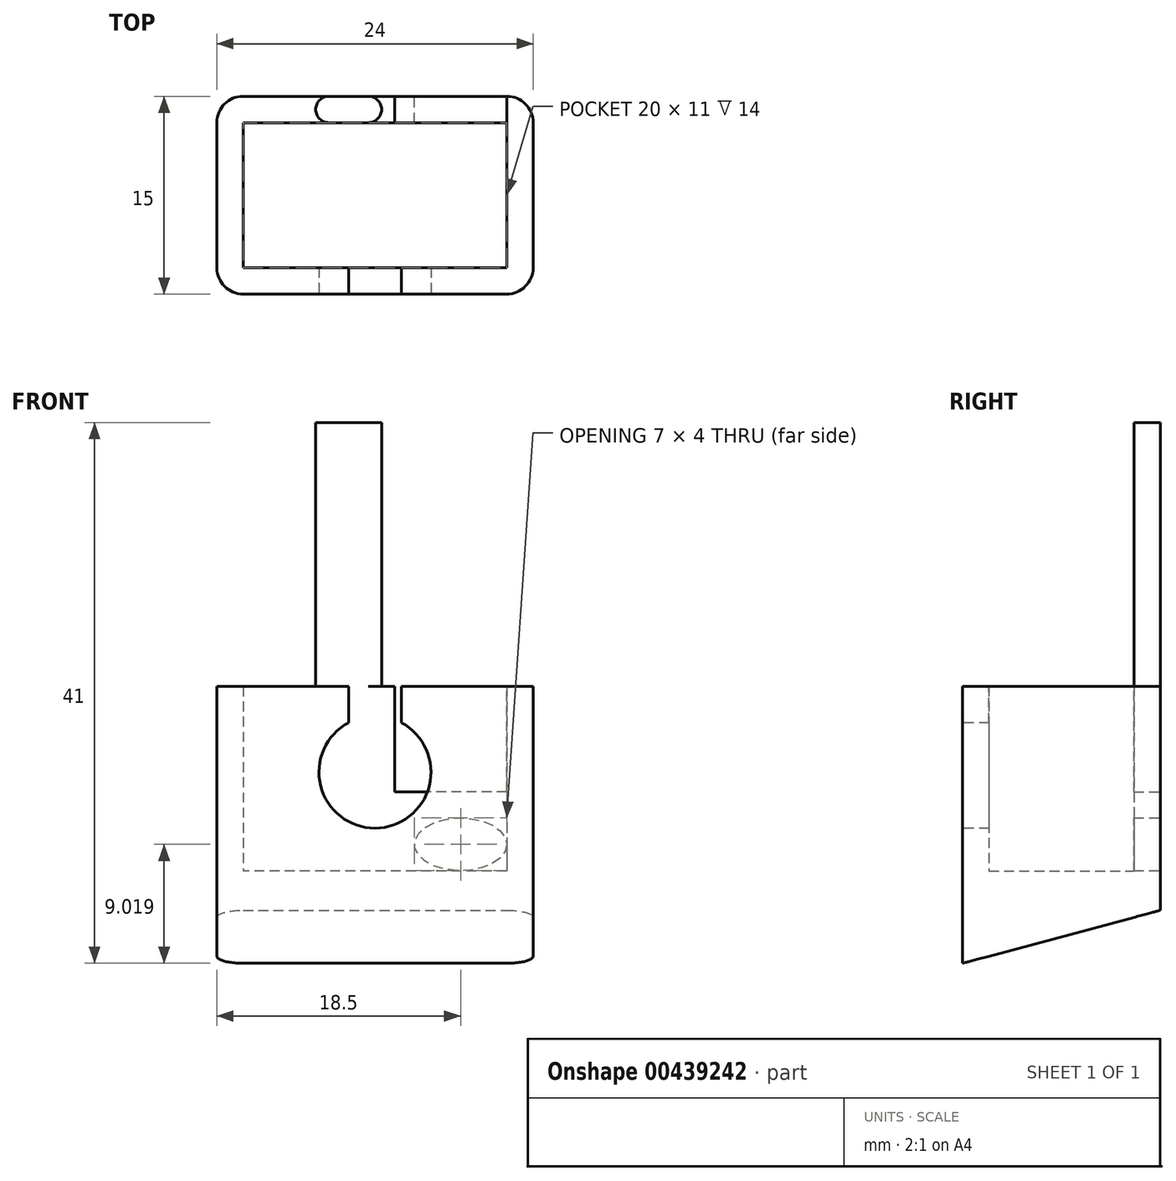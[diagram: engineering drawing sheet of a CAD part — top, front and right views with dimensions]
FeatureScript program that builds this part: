
annotation { "Feature Type Name" : "Feature", "Feature Type Description" : "" }
export const myFeature = defineFeature(function(context is Context, id is Id, definition is map)
    precondition{}
    {
        {
            var Q0;
            Q0=qCreatedBy(makeId("Top.planeOp"),FACE);
            var sketch = newSketch(context, id + "F0", { "sketchPlane" : qUnion([Q0])});
            skLineSegment(sketch, "E0.bottom", {"start": v(12, -7.5) * mm, "end": v(-12, -7.5) * mm});
            skLineSegment(sketch, "E0.top", {"start": v(12, 7.5) * mm, "end": v(-12, 7.5) * mm});
            skLineSegment(sketch, "E0.left", {"start": v(12, -7.5) * mm, "end": v(12, 7.5) * mm});
            skLineSegment(sketch, "E0.right", {"start": v(-12, -7.5) * mm, "end": v(-12, 7.5) * mm});
            skPoint(sketch, "E0.middle", {"position": v(0, 0) * mm});
            skSolve(sketch);
        }
        {
            var Q0;
            Q0=qSketchRegion(id+"F0",true);
            extrude(context, id + "F1", {"entities" : qUnion([Q0]), "depth" : 16 * mm, "offsetDistance" : 25 * mm});
        }
        {
            var Q0;
            Q0=makeQuery(id+"F1.opExtrude","CAP_FACE",FACE,{"disambiguationData":[OSD([sQuery(id+"F0.wireOp",EDGE,"E0.bottom"),sQuery(id+"F0.wireOp",EDGE,"E0.top"),sQuery(id+"F0.wireOp",EDGE,"E0.left"),sQuery(id+"F0.wireOp",EDGE,"E0.right")])],"isStart":false});
            shell(context, id + "F2", {"entities" : qUnion([Q0]), "thickness" : 2 * mm});
        }
        {
            var Q0;
            Q0=makeQuery(id+"F1.opExtrude","SWEPT_FACE",FACE,{"disambiguationData":[OSD([sQuery(id+"F0.wireOp",EDGE,"E0.bottom")])]});
            var sketch = newSketch(context, id + "F3", { "sketchPlane" : qUnion([Q0])});
            skArc(sketch, "E1", {"start": v(-2, 13.25) * mm, "mid": v(0, 5.25) * mm, "end": v(2, 13.25) * mm});
            skLineSegment(sketch, "E2", {"start": v(-2, 13.25) * mm, "end": v(-2, 16) * mm});
            skLineSegment(sketch, "E3.MirrorCS", {"start": v(2, 13.25) * mm, "end": v(2, 16) * mm});
            skSolve(sketch);
        }
        {
            var Q0;
            Q0=makeQuery(id+"F3.imprint","IMPRINT",FACE,{"disambiguationData":[TD([[makeQuery(id+"F3.imprint","IMPRINT",EDGE,{"derivedFrom":sQuery(id+"F3.wireOp",EDGE,"E1")}),1.0]])]});
            extrude(context, id + "F4", {"entities" : qUnion([Q0]), "operationType" : NewBodyOperationType.REMOVE, "oppositeDirection" : true, "depth" : 5 * mm, "offsetDistance" : 25 * mm});
        }
        {
            var Q0;
            Q0=makeQuery(id+"F1.opExtrude","CAP_FACE",FACE,{"disambiguationData":[OSD([sQuery(id+"F0.wireOp",EDGE,"E0.bottom"),sQuery(id+"F0.wireOp",EDGE,"E0.top"),sQuery(id+"F0.wireOp",EDGE,"E0.left"),sQuery(id+"F0.wireOp",EDGE,"E0.right")])],"isStart":false});
            var sketch = newSketch(context, id + "F5", { "sketchPlane" : qUnion([Q0])});
            skLineSegment(sketch, "E4.bottom", {"start": v(-4.5, 7.5) * mm, "end": v(0.5, 7.5) * mm});
            skLineSegment(sketch, "E4.top", {"start": v(-4.5, 5.5) * mm, "end": v(0.5, 5.5) * mm});
            skLineSegment(sketch, "E4.left", {"start": v(-4.5, 7.5) * mm, "end": v(-4.5, 5.5) * mm});
            skLineSegment(sketch, "E4.right", {"start": v(0.5, 7.5) * mm, "end": v(0.5, 5.5) * mm});
            skSolve(sketch);
        }
        {
            var Q0;
            Q0=makeQuery(id+"F5.imprint","IMPRINT",FACE,{"disambiguationData":[TD([[makeQuery(id+"F5.imprint","IMPRINT",EDGE,{"derivedFrom":sQuery(id+"F5.wireOp",EDGE,"E4.bottom")}),1.0]])]});
            extrude(context, id + "F6", {"entities" : qUnion([Q0]), "operationType" : NewBodyOperationType.ADD, "depth" : 20 * mm, "offsetDistance" : 25 * mm});
        }
        {
            var Q0;
            Q0=makeQuery(id+"F6.opExtrude","SWEPT_EDGE",EDGE,{"disambiguationData":[OSD([sQuery(id+"F0.wireOp",EDGE,"E0.top"),sQuery(id+"F5.wireOp",EDGE,"E4.top"),sQuery(id+"F5.wireOp",EDGE,"E4.right")])]});
            var Q1;
            Q1=makeQuery(id+"F6.opExtrude","SWEPT_EDGE",EDGE,{"disambiguationData":[OSD([sQuery(id+"F0.wireOp",EDGE,"E0.top"),sQuery(id+"F5.wireOp",EDGE,"E4.bottom"),sQuery(id+"F5.wireOp",EDGE,"E4.right")])]});
            var Q2;
            Q2=makeQuery(id+"F6.opExtrude","SWEPT_EDGE",EDGE,{"disambiguationData":[OSD([sQuery(id+"F0.wireOp",EDGE,"E0.top"),sQuery(id+"F5.wireOp",EDGE,"E4.top"),sQuery(id+"F5.wireOp",EDGE,"E4.left")])]});
            var Q3;
            Q3=makeQuery(id+"F6.opExtrude","SWEPT_EDGE",EDGE,{"disambiguationData":[OSD([sQuery(id+"F0.wireOp",EDGE,"E0.top"),sQuery(id+"F5.wireOp",EDGE,"E4.bottom"),sQuery(id+"F5.wireOp",EDGE,"E4.left")])]});
            fillet(context, id + "F7", {"entities" : qUnion([Q0, Q1, Q2, Q3]), "radius" : 1 * mm, "tangentPropagation" : true, "allowEdgeOverflow" : false});
        }
        {
            var Q0;
            {var subQ0=sQuery(id+"F0.wireOp",EDGE,"E0.bottom");var subQ1=sQuery(id+"F0.wireOp",EDGE,"E0.left");var subQ2=sQuery(id+"F0.wireOp",EDGE,"E0.top");Q0=makeQuery(id+"F6.boolean.opBoolean","SPLIT",FACE,{"disambiguationData":[TD([makeQuery(id+"F1.opExtrude","SWEPT_FACE",FACE,{"disambiguationData":[OSD([subQ1])]})])],"derivedFrom":makeQuery(id+"F1.opExtrude","CAP_FACE",FACE,{"disambiguationData":[OSD([subQ0,subQ2,subQ1,sQuery(id+"F0.wireOp",EDGE,"E0.right")])],"isStart":false})});}
            var sketch = newSketch(context, id + "F8", { "sketchPlane" : qUnion([Q0])});
            skLineSegment(sketch, "E5.bottom", {"start": v(10, 5.5) * mm, "end": v(1.5, 5.5) * mm});
            skLineSegment(sketch, "E5.top", {"start": v(10, 7.5) * mm, "end": v(1.5, 7.5) * mm});
            skLineSegment(sketch, "E5.left", {"start": v(10, 5.5) * mm, "end": v(10, 7.5) * mm});
            skLineSegment(sketch, "E5.right", {"start": v(1.5, 5.5) * mm, "end": v(1.5, 7.5) * mm});
            skSolve(sketch);
        }
        {
            var Q0;
            Q0=qSketchRegion(id+"F8",true);
            extrude(context, id + "F9", {"entities" : qUnion([Q0]), "operationType" : NewBodyOperationType.REMOVE, "oppositeDirection" : true, "depth" : 8 * mm, "offsetDistance" : 25 * mm});
        }
        {
            var Q0;
            Q0=makeQuery(id+"F1.opExtrude","CAP_FACE",FACE,{"disambiguationData":[OSD([sQuery(id+"F0.wireOp",EDGE,"E0.bottom"),sQuery(id+"F0.wireOp",EDGE,"E0.top"),sQuery(id+"F0.wireOp",EDGE,"E0.left"),sQuery(id+"F0.wireOp",EDGE,"E0.right")])],"isStart":true});
            extrude(context, id + "F10", {"entities" : qUnion([Q0]), "operationType" : NewBodyOperationType.ADD, "depth" : 5 * mm, "offsetDistance" : 25 * mm});
        }
        {
            var Q0;
            {var subQ0=sQuery(id+"F0.wireOp",EDGE,"E0.left");Q0=makeQuery(id+"F10.boolean.opBoolean","MERGE",FACE,{"derivedFrom":[makeQuery(id+"F1.opExtrude","SWEPT_FACE",FACE,{"disambiguationData":[OSD([subQ0])]}),makeQuery(id+"F10.opExtrude","SWEPT_FACE",FACE,{"disambiguationData":[OSD([subQ0])]})]});}
            var sketch = newSketch(context, id + "F11", { "sketchPlane" : qUnion([Q0])});
            skLineSegment(sketch, "E6", {"start": v(-7.5, -5) * mm, "end": v(7.5, -0.98) * mm});
            skSolve(sketch);
        }
        {
            var Q0;
            {var subQ0=sQuery(id+"F11.wireOp",EDGE,"E6");Q0=makeQuery(id+"F11.imprint","IMPRINT",FACE,{"disambiguationData":[TD([[makeQuery(id+"F11.imprint","IMPRINT",EDGE,{"derivedFrom":subQ0}),-1.0]])]});}
            extrude(context, id + "F12", {"entities" : qUnion([Q0]), "operationType" : NewBodyOperationType.REMOVE, "oppositeDirection" : true, "depth" : 25 * mm, "offsetDistance" : 25 * mm});
        }
        {
            var Q0;
            Q0=makeQuery(id+"F1.opExtrude","SWEPT_EDGE",EDGE,{"disambiguationData":[OSD([sQuery(id+"F0.wireOp",EDGE,"E0.bottom"),sQuery(id+"F0.wireOp",EDGE,"E0.left")])]});
            var Q1;
            Q1=makeQuery(id+"F1.opExtrude","SWEPT_EDGE",EDGE,{"disambiguationData":[OSD([sQuery(id+"F0.wireOp",EDGE,"E0.bottom"),sQuery(id+"F0.wireOp",EDGE,"E0.right")])]});
            var Q2;
            Q2=makeQuery(id+"F1.opExtrude","SWEPT_EDGE",EDGE,{"disambiguationData":[OSD([sQuery(id+"F0.wireOp",EDGE,"E0.top"),sQuery(id+"F0.wireOp",EDGE,"E0.right")])]});
            var Q3;
            {var subQ0=sQuery(id+"F0.wireOp",EDGE,"E0.left");var subQ1=sQuery(id+"F0.wireOp",EDGE,"E0.top");Q3=makeQuery(id+"FvEb3cs1EhIj02q_1.boolean.opBoolean","SPLIT",EDGE,{"disambiguationData":[TD([makeQuery(id+"F1.opExtrude","CAP_FACE",FACE,{"disambiguationData":[OSD([sQuery(id+"F0.wireOp",EDGE,"E0.bottom"),subQ1,subQ0,sQuery(id+"F0.wireOp",EDGE,"E0.right")])],"isStart":false})])],"derivedFrom":makeQuery(id+"F1.opExtrude","SWEPT_EDGE",EDGE,{"disambiguationData":[OSD([subQ1,subQ0])]})});}
            var Q4;
            {var subQ0=sQuery(id+"F0.wireOp",EDGE,"E0.left");var subQ1=sQuery(id+"F0.wireOp",EDGE,"E0.top");Q4=makeQuery(id+"FvEb3cs1EhIj02q_1.boolean.opBoolean","SPLIT",EDGE,{"disambiguationData":[TD([makeQuery(id+"F1.opExtrude","CAP_FACE",FACE,{"disambiguationData":[OSD([sQuery(id+"F0.wireOp",EDGE,"E0.bottom"),subQ1,subQ0,sQuery(id+"F0.wireOp",EDGE,"E0.right")])],"isStart":true})])],"derivedFrom":makeQuery(id+"F1.opExtrude","SWEPT_EDGE",EDGE,{"disambiguationData":[OSD([subQ1,subQ0])]})});}
            fillet(context, id + "F13", {"entities" : qUnion([Q0, Q1, Q2, Q3, Q4]), "radius" : 2 * mm, "tangentPropagation" : true, "allowEdgeOverflow" : false});
        }
        {
            var Q0;
            Q0=makeQuery(id+"F6.boolean.opBoolean","MERGE",FACE,{"derivedFrom":[makeQuery(id+"F1.opExtrude","SWEPT_FACE",FACE,{"disambiguationData":[OSD([sQuery(id+"F0.wireOp",EDGE,"E0.top")])]}),makeQuery(id+"F6.opExtrude","SWEPT_FACE",FACE,{"disambiguationData":[OSD([sQuery(id+"F5.wireOp",EDGE,"E4.bottom")])]})]});
            var sketch = newSketch(context, id + "F14", { "sketchPlane" : qUnion([Q0])});
            skEllipse(sketch, "E7", {"center": v(-6.5, 4.02) * mm, "majorRadius": 3.5 * mm, "minorRadius": 2 * mm, "majorAxis": v(1, 0)});
            skLineSegment(sketch, "E8", {"start": v(-10, 4.02) * mm, "end": v(-10, 4.02) * mm});
            skPoint(sketch, "E8.endSnap0", {"position": v(-10, 3.5) * mm});
            skLineSegment(sketch, "E9", {"start": v(-6.5, 2.02) * mm, "end": v(-6.5, -0.98) * mm, "construction": true});
            skSolve(sketch);
        }
        {
            var Q0;
            Q0=makeQuery(id+"F14.imprint","IMPRINT",FACE,{"disambiguationData":[TD([[makeQuery(id+"F14.imprint","IMPRINT",EDGE,{"derivedFrom":sQuery(id+"F14.wireOp",EDGE,"E7")}),1.0]])]});
            extrude(context, id + "F15", {"entities" : qUnion([Q0]), "operationType" : NewBodyOperationType.REMOVE, "oppositeDirection" : true, "depth" : 2 * mm});
        }
    });
